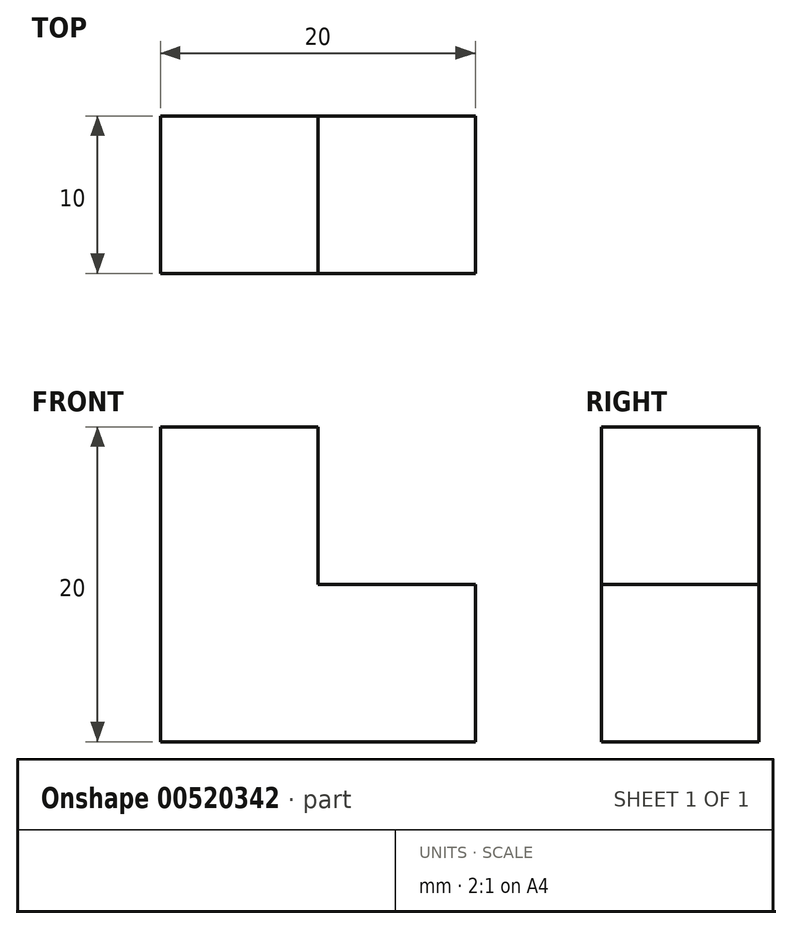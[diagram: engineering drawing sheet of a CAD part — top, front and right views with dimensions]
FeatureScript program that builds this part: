
annotation { "Feature Type Name" : "Feature", "Feature Type Description" : "" }
export const myFeature = defineFeature(function(context is Context, id is Id, definition is map)
    precondition{}
    {
        {
            var Q0;
            Q0=qCreatedBy(makeId("Front.planeOp"),FACE);
            var sketch = newSketch(context, id + "F0", { "sketchPlane" : qUnion([Q0])});
            skLineSegment(sketch, "E0", {"start": v(0, 0) * mm, "end": v(0, 20) * mm});
            skLineSegment(sketch, "E1", {"start": v(0, 20) * mm, "end": v(10, 20) * mm});
            skLineSegment(sketch, "E2", {"start": v(10, 20) * mm, "end": v(10, 10) * mm});
            skLineSegment(sketch, "E3", {"start": v(10, 10) * mm, "end": v(20, 10) * mm});
            skLineSegment(sketch, "E4", {"start": v(20, 10) * mm, "end": v(20, 0) * mm});
            skLineSegment(sketch, "E5", {"start": v(20, 0) * mm, "end": v(0, 0) * mm});
            skSolve(sketch);
        }
        {
            var Q0;
            Q0=makeQuery(id+"F0.imprint","IMPRINT",FACE,{"disambiguationData":[TD([[makeQuery(id+"F0.imprint","IMPRINT",EDGE,{"derivedFrom":sQuery(id+"F0.wireOp",EDGE,"E0")}),-1.0]])]});
            extrude(context, id + "F1", {"entities" : qUnion([Q0]), "depth" : 10 * mm, "offsetDistance" : 25 * mm});
        }
    });
